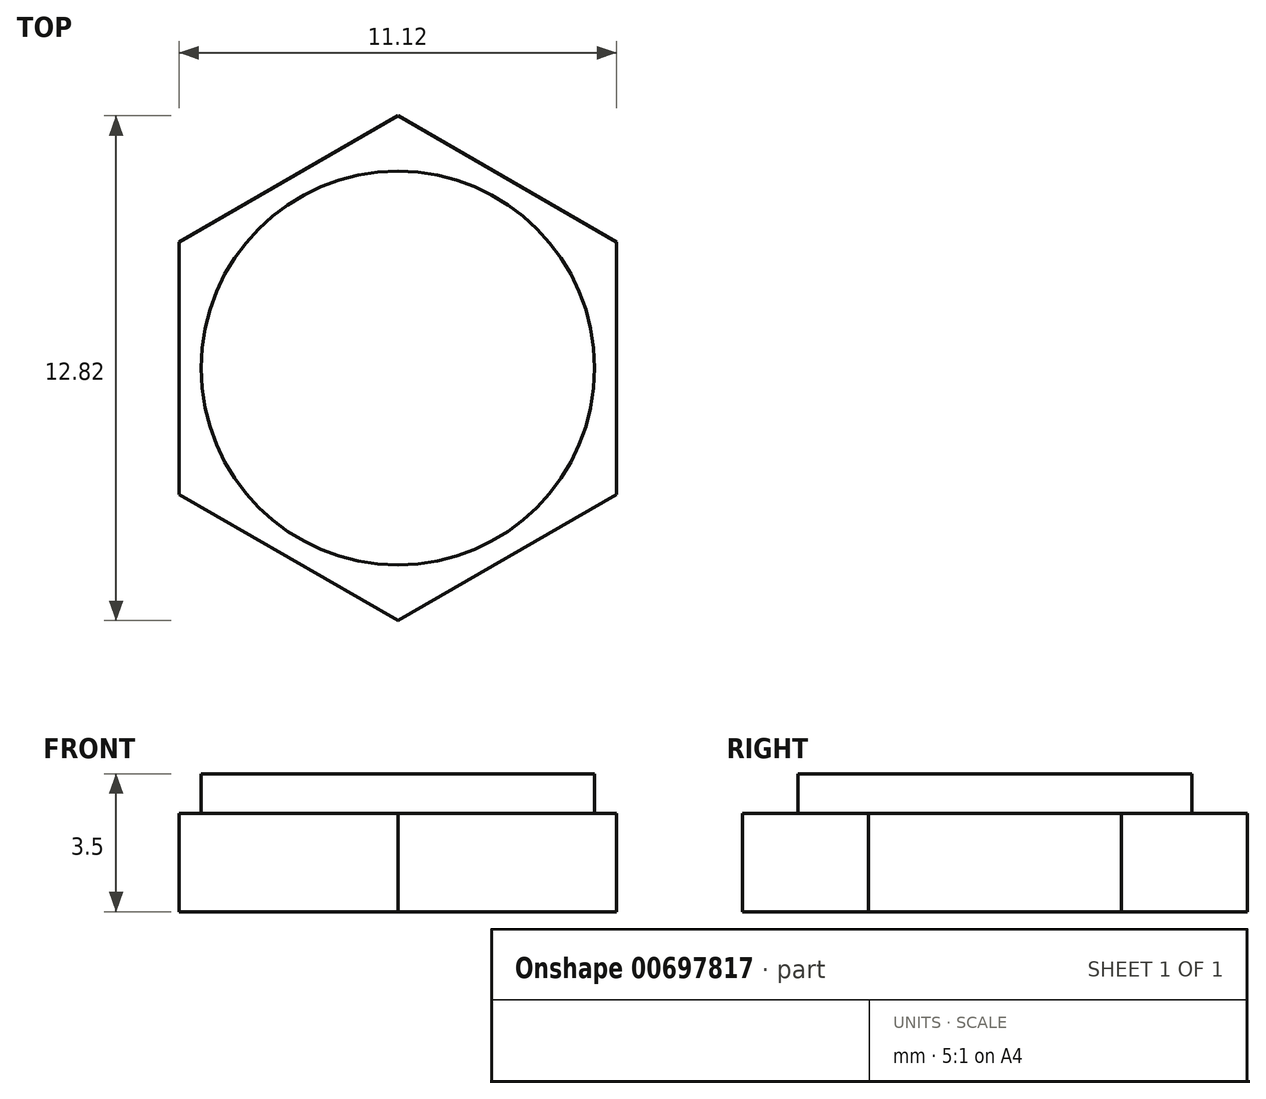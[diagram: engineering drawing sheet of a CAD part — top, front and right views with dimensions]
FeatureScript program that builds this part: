
annotation { "Feature Type Name" : "Feature", "Feature Type Description" : "" }
export const myFeature = defineFeature(function(context is Context, id is Id, definition is map)
    precondition{}
    {
        {
            var Q0;
            Q0=qCreatedBy(makeId("Top.planeOp"),FACE);
            var sketch = newSketch(context, id + "F0", { "sketchPlane" : qUnion([Q0])});
            skCircle(sketch, "E0.cCircle", {"center": v(0, 0) * mm, "radius": 5.55 * mm, "construction": true});
            skLineSegment(sketch, "E0.0", {"start": v(-5.55, -3.2) * mm, "end": v(-5.55, 3.2) * mm});
            skLineSegment(sketch, "E0.1", {"start": v(-5.55, 3.2) * mm, "end": v(0, 6.41) * mm});
            skLineSegment(sketch, "E0.2", {"start": v(0, 6.41) * mm, "end": v(5.55, 3.2) * mm});
            skLineSegment(sketch, "E0.3", {"start": v(5.55, 3.2) * mm, "end": v(5.56, -3.2) * mm});
            skLineSegment(sketch, "E0.4", {"start": v(5.56, -3.2) * mm, "end": v(0, -6.41) * mm});
            skLineSegment(sketch, "E0.5", {"start": v(0, -6.41) * mm, "end": v(-5.55, -3.2) * mm});
            skPoint(sketch, "E0.0.midPoint", {"position": v(-5.55, 0) * mm});
            skCircle(sketch, "E1", {"center": v(0, 0) * mm, "radius": 5 * mm});
            skSolve(sketch);
        }
        {
            var Q0;
            Q0=qSketchRegion(id+"F0",true);
            var Q1;
            Q1=makeQuery(id+"F0.imprint","IMPRINT",FACE,{"disambiguationData":[TD([[makeQuery(id+"F0.imprint","IMPRINT",EDGE,{"derivedFrom":sQuery(id+"F0.wireOp",EDGE,"E1")}),1.0]])]});
            extrude(context, id + "F1", {"entities" : qUnion([Q0, Q1]), "depth" : 2.5 * mm, "offsetDistance" : 25 * mm});
        }
        {
            var Q0;
            Q0=makeQuery(id+"F0.imprint","IMPRINT",FACE,{"disambiguationData":[TD([[makeQuery(id+"F0.imprint","IMPRINT",EDGE,{"derivedFrom":sQuery(id+"F0.wireOp",EDGE,"E1")}),1.0]])]});
            extrude(context, id + "F2", {"entities" : qUnion([Q0]), "operationType" : NewBodyOperationType.ADD, "depth" : 3.5 * mm, "offsetDistance" : 25 * mm});
        }
    });
